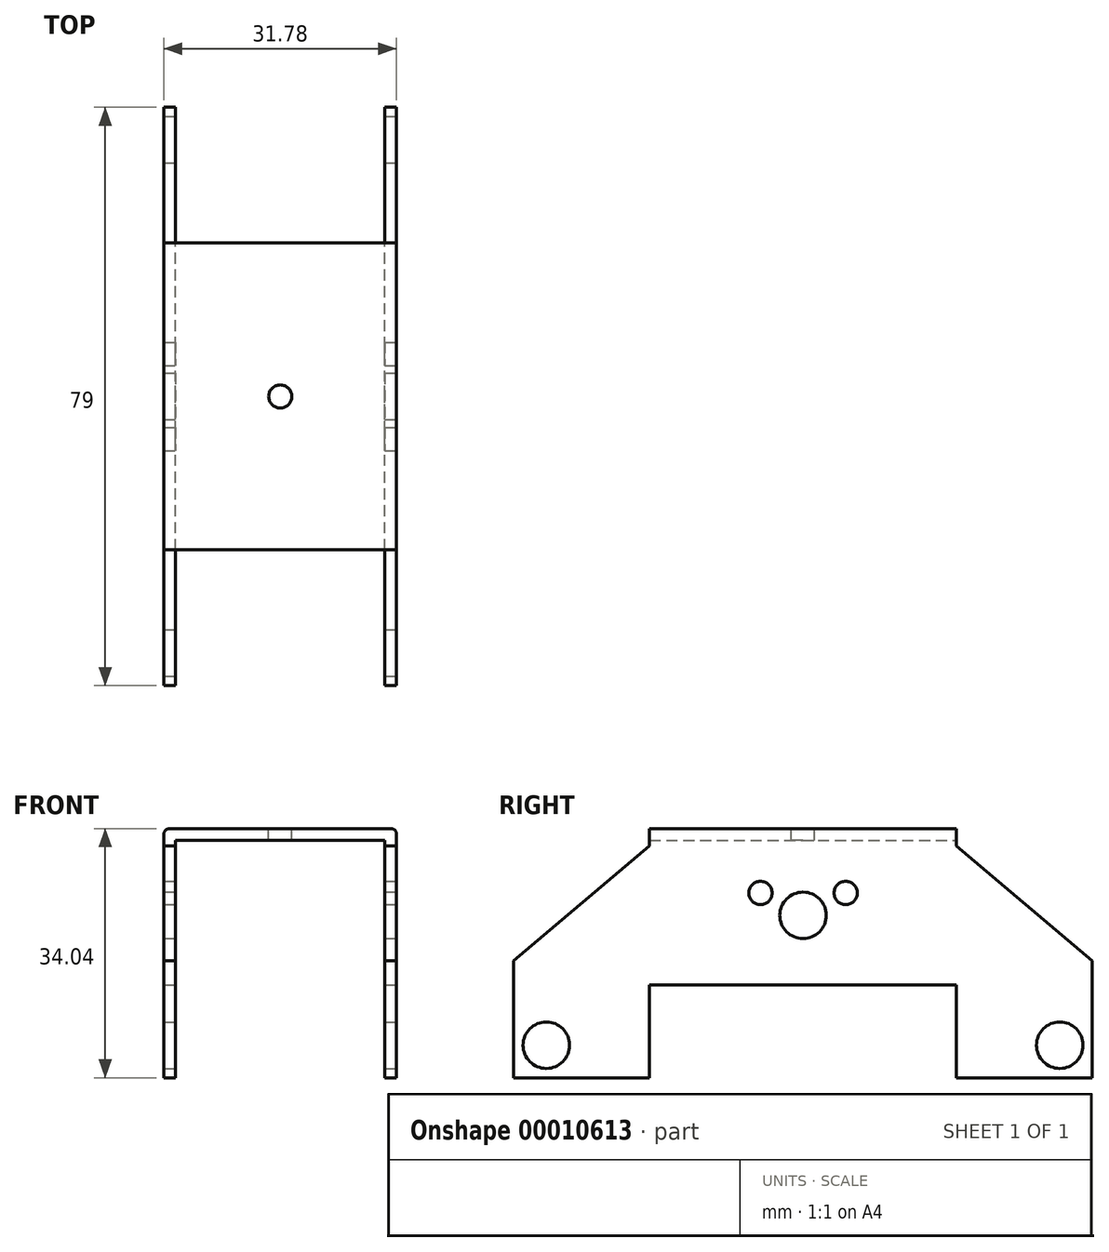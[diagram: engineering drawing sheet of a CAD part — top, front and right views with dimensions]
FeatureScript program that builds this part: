
annotation { "Feature Type Name" : "Feature", "Feature Type Description" : "" }
export const myFeature = defineFeature(function(context is Context, id is Id, definition is map)
    precondition{}
    {
        {
            var Q0;
            Q0=qCreatedBy(makeId("Right.planeOp"),FACE);
            var sketch = newSketch(context, id + "F0", { "sketchPlane" : qUnion([Q0])});
            skLineSegment(sketch, "E0.rect.bottom", {"start": v(39.5, -17.02) * mm, "end": v(20.96, -17.02) * mm});
            skLineSegment(sketch, "E0.rect.top", {"start": v(20.95, 14.63) * mm, "end": v(-20.96, 14.63) * mm});
            skLineSegment(sketch, "E0.rect.left", {"start": v(39.5, -17.02) * mm, "end": v(39.5, -1.02) * mm});
            skLineSegment(sketch, "E0.rect.right", {"start": v(-39.5, -17.02) * mm, "end": v(-39.5, -1.02) * mm});
            skPoint(sketch, "E0.rect.middle", {"position": v(0, 0) * mm});
            skLineSegment(sketch, "E1", {"start": v(-39.5, -4.32) * mm, "end": v(39.5, -4.32) * mm, "construction": true});
            skLineSegment(sketch, "E2", {"start": v(-20.96, 14.63) * mm, "end": v(-20.96, -17.02) * mm, "construction": true});
            skLineSegment(sketch, "E3", {"start": v(20.95, 14.63) * mm, "end": v(20.96, -17.02) * mm, "construction": true});
            skLineSegment(sketch, "E4", {"start": v(-39.5, -1.02) * mm, "end": v(39.5, -1.02) * mm, "construction": true});
            skLineSegment(sketch, "E5", {"start": v(39.5, -1.02) * mm, "end": v(20.95, 14.63) * mm});
            skLineSegment(sketch, "E6", {"start": v(-39.5, -1.02) * mm, "end": v(-20.96, 14.63) * mm});
            skLineSegment(sketch, "E7.trimOffspring", {"start": v(-20.95, -17.02) * mm, "end": v(-39.5, -17.02) * mm});
            skLineSegment(sketch, "E8", {"start": v(-20.96, -17.02) * mm, "end": v(-20.96, -4.32) * mm});
            skLineSegment(sketch, "E9", {"start": v(-20.96, -4.32) * mm, "end": v(20.96, -4.32) * mm});
            skLineSegment(sketch, "E10", {"start": v(20.96, -4.32) * mm, "end": v(20.96, -17.02) * mm});
            skLineSegment(sketch, "E11.bottom", {"start": v(-20.96, 14.63) * mm, "end": v(20.95, 14.63) * mm});
            skLineSegment(sketch, "E11.top", {"start": v(-20.96, 15.42) * mm, "end": v(20.95, 15.42) * mm});
            skLineSegment(sketch, "E11.left", {"start": v(-20.96, 14.63) * mm, "end": v(-20.96, 15.42) * mm});
            skLineSegment(sketch, "E11.right", {"start": v(20.95, 14.63) * mm, "end": v(20.95, 15.42) * mm});
            skLineSegment(sketch, "E12.top", {"start": v(-20.96, 17.02) * mm, "end": v(20.95, 17.02) * mm});
            skLineSegment(sketch, "E12.left", {"start": v(-20.96, 15.42) * mm, "end": v(-20.96, 17.02) * mm});
            skLineSegment(sketch, "E12.right", {"start": v(20.95, 15.42) * mm, "end": v(20.95, 17.02) * mm});
            skCircle(sketch, "E13", {"center": v(0, 5.16) * mm, "radius": 3.18 * mm});
            skCircle(sketch, "E14", {"center": v(-35.05, -12.57) * mm, "radius": 3.18 * mm});
            skCircle(sketch, "E15", {"center": v(5.82, 8.21) * mm, "radius": 1.59 * mm});
            skLineSegment(sketch, "E16", {"start": v(0, 17.02) * mm, "end": v(0, -4.32) * mm, "construction": true});
            skCircle(sketch, "E17.0.MirrorC", {"center": v(-5.82, 8.21) * mm, "radius": 1.59 * mm});
            skCircle(sketch, "E18.0.MirrorC", {"center": v(35.05, -12.57) * mm, "radius": 3.18 * mm});
            skSolve(sketch);
        }
        {
            var Q0;
            Q0=qSketchRegion(id+"F0",true);
            extrude(context, id + "F1", {"entities" : qUnion([Q0]), "oppositeDirection" : true, "depth" : 1.57 * mm});
        }
        {
            var Q0;
            Q0=qSketchRegion(id+"F0",true);
            extrude(context, id + "F2", {"entities" : qUnion([Q0]), "operationType" : NewBodyOperationType.ADD, "oppositeDirection" : true, "depth" : 1.6 * mm});
        }
        {
            var Q0;
            Q0=makeQuery(id+"F2.opExtrude","CAP_FACE",FACE,{"disambiguationData":[OSD([sQuery(id+"F0.wireOp",EDGE,"E0.rect.bottom"),sQuery(id+"F0.wireOp",EDGE,"E0.rect.left"),sQuery(id+"F0.wireOp",EDGE,"E0.rect.right"),sQuery(id+"F0.wireOp",EDGE,"E5"),sQuery(id+"F0.wireOp",EDGE,"E6"),sQuery(id+"F0.wireOp",EDGE,"E7.trimOffspring"),sQuery(id+"F0.wireOp",EDGE,"E8"),sQuery(id+"F0.wireOp",EDGE,"E9"),sQuery(id+"F0.wireOp",EDGE,"E10"),sQuery(id+"F0.wireOp",EDGE,"E11.left"),sQuery(id+"F0.wireOp",EDGE,"E11.right"),sQuery(id+"F0.wireOp",EDGE,"E12.top"),sQuery(id+"F0.wireOp",EDGE,"E12.left"),sQuery(id+"F0.wireOp",EDGE,"E12.right")])],"isStart":false});
            var sketch = newSketch(context, id + "F3", { "sketchPlane" : qUnion([Q0])});
            skLineSegment(sketch, "E19.0", {"start": v(20.96, 17.02) * mm, "end": v(-20.95, 17.02) * mm});
            skLineSegment(sketch, "E20.0", {"start": v(20.96, 15.42) * mm, "end": v(-20.95, 15.42) * mm});
            skLineSegment(sketch, "E21.0", {"start": v(-20.95, 15.42) * mm, "end": v(-20.95, 17.02) * mm});
            skLineSegment(sketch, "E22.0", {"start": v(20.96, 15.42) * mm, "end": v(20.96, 17.02) * mm});
            skSolve(sketch);
        }
        {
            var Q0;
            Q0=qSketchRegion(id+"F3",true);
            extrude(context, id + "F4", {"entities" : qUnion([Q0]), "operationType" : NewBodyOperationType.ADD, "depth" : 28.57 * mm});
        }
        {
            var Q0;
            Q0=makeQuery(id+"F4.opExtrude","CAP_FACE",FACE,{"disambiguationData":[OSD([sQuery(id+"F3.wireOp",EDGE,"E19.0"),sQuery(id+"F3.wireOp",EDGE,"E20.0"),sQuery(id+"F3.wireOp",EDGE,"E21.0"),sQuery(id+"F3.wireOp",EDGE,"E22.0")])],"isStart":false});
            var sketch = newSketch(context, id + "F5", { "sketchPlane" : qUnion([Q0])});
            skLineSegment(sketch, "E23.0", {"start": v(20.96, -4.32) * mm, "end": v(-20.96, -4.32) * mm});
            skLineSegment(sketch, "E24.0", {"start": v(20.96, -17.02) * mm, "end": v(20.96, -4.32) * mm});
            skLineSegment(sketch, "E25.0", {"start": v(20.95, -17.02) * mm, "end": v(39.5, -17.02) * mm});
            skLineSegment(sketch, "E26.0", {"start": v(39.5, -17.02) * mm, "end": v(39.5, -1.02) * mm});
            skLineSegment(sketch, "E27.0", {"start": v(39.5, -1.02) * mm, "end": v(20.96, 14.63) * mm});
            skLineSegment(sketch, "E28.0", {"start": v(20.96, 14.63) * mm, "end": v(20.96, 15.42) * mm});
            skLineSegment(sketch, "E29.0", {"start": v(20.96, 15.42) * mm, "end": v(20.96, 17.02) * mm});
            skLineSegment(sketch, "E30.0", {"start": v(20.96, 17.02) * mm, "end": v(-20.95, 17.02) * mm});
            skLineSegment(sketch, "E31.0", {"start": v(-20.95, 15.42) * mm, "end": v(-20.95, 17.02) * mm});
            skLineSegment(sketch, "E32.0", {"start": v(-20.95, 14.63) * mm, "end": v(-20.95, 15.42) * mm});
            skLineSegment(sketch, "E33.0", {"start": v(-39.5, -1.02) * mm, "end": v(-20.95, 14.63) * mm});
            skLineSegment(sketch, "E34.0", {"start": v(-39.5, -17.02) * mm, "end": v(-39.5, -1.02) * mm});
            skLineSegment(sketch, "E35.0", {"start": v(-39.5, -17.02) * mm, "end": v(-20.96, -17.02) * mm});
            skLineSegment(sketch, "E36.0", {"start": v(-20.96, -4.32) * mm, "end": v(-20.96, -17.02) * mm});
            skCircle(sketch, "E37.0", {"center": v(-5.82, 8.21) * mm, "radius": 1.59 * mm});
            skCircle(sketch, "E38.0", {"center": v(0, 5.16) * mm, "radius": 3.18 * mm});
            skCircle(sketch, "E39.0", {"center": v(5.82, 8.21) * mm, "radius": 1.59 * mm});
            skCircle(sketch, "E40.0", {"center": v(35.05, -12.57) * mm, "radius": 3.18 * mm});
            skLineSegment(sketch, "E41.0", {"start": v(0, 17.02) * mm, "end": v(0, -4.32) * mm, "construction": true});
            skCircle(sketch, "E42.0", {"center": v(-35.05, -12.57) * mm, "radius": 3.18 * mm});
            skSolve(sketch);
        }
        {
            var Q0;
            Q0=qSketchRegion(id+"F5",true);
            extrude(context, id + "F6", {"entities" : qUnion([Q0]), "operationType" : NewBodyOperationType.ADD, "depth" : 1.6 * mm});
        }
        {
            var Q0;
            Q0=makeQuery(id+"F4.opExtrude","CAP_EDGE",EDGE,{"disambiguationData":[OSD([sQuery(id+"F3.wireOp",EDGE,"E20.0")])],"isStart":true});
            var Q1;
            Q1=makeQuery(id+"F4.opExtrude","CAP_EDGE",EDGE,{"disambiguationData":[OSD([sQuery(id+"F3.wireOp",EDGE,"E20.0")])],"isStart":false});
            var Q2;
            Q2=makeQuery(id+"F6.opExtrude","CAP_EDGE",EDGE,{"disambiguationData":[OSD([sQuery(id+"F5.wireOp",EDGE,"E30.0")])],"isStart":false});
            var Q3;
            Q3=makeQuery(id+"F1.opExtrude","CAP_EDGE",EDGE,{"disambiguationData":[OSD([sQuery(id+"F0.wireOp",EDGE,"E12.top")])],"isStart":true});
            fillet(context, id + "F7", {"entities" : qUnion([Q0, Q1, Q2, Q3]), "radius" : 0.79 * mm, "tangentPropagation" : true, "allowEdgeOverflow" : false});
        }
        {
            var Q0;
            {var subQ0=sQuery(id+"F0.wireOp",EDGE,"E12.top");Q0=makeQuery(id+"F6.boolean.opBoolean","MERGE",FACE,{"derivedFrom":[makeQuery(id+"F4.boolean.opBoolean","MERGE",FACE,{"derivedFrom":[makeQuery(id+"F2.boolean.opBoolean","MERGE",FACE,{"derivedFrom":[makeQuery(id+"F1.opExtrude","SWEPT_FACE",FACE,{"disambiguationData":[OSD([subQ0])]}),makeQuery(id+"F2.opExtrude","SWEPT_FACE",FACE,{"disambiguationData":[OSD([subQ0])]})]}),makeQuery(id+"F4.opExtrude","SWEPT_FACE",FACE,{"disambiguationData":[OSD([sQuery(id+"F3.wireOp",EDGE,"E19.0")])]})]}),makeQuery(id+"F6.opExtrude","SWEPT_FACE",FACE,{"disambiguationData":[OSD([sQuery(id+"F5.wireOp",EDGE,"E30.0")])]})]});}
            var sketch = newSketch(context, id + "F8", { "sketchPlane" : qUnion([Q0])});
            skLineSegment(sketch, "E43.0", {"start": v(0, -20.96) * mm, "end": v(0, 20.95) * mm, "construction": true});
            skLineSegment(sketch, "E44.0", {"start": v(-30.99, -20.96) * mm, "end": v(-0.79, -20.96) * mm, "construction": true});
            skCircle(sketch, "E45", {"center": v(-15.88, 0) * mm, "radius": 1.59 * mm});
            skSolve(sketch);
        }
        {
            var Q0;
            Q0=qSketchRegion(id+"F8",true);
            extrude(context, id + "F9", {"entities" : qUnion([Q0]), "operationType" : NewBodyOperationType.REMOVE, "endBound" : BoundingType.UP_TO_NEXT, "oppositeDirection" : true, "depth" : 5.08 * mm});
        }
    });
